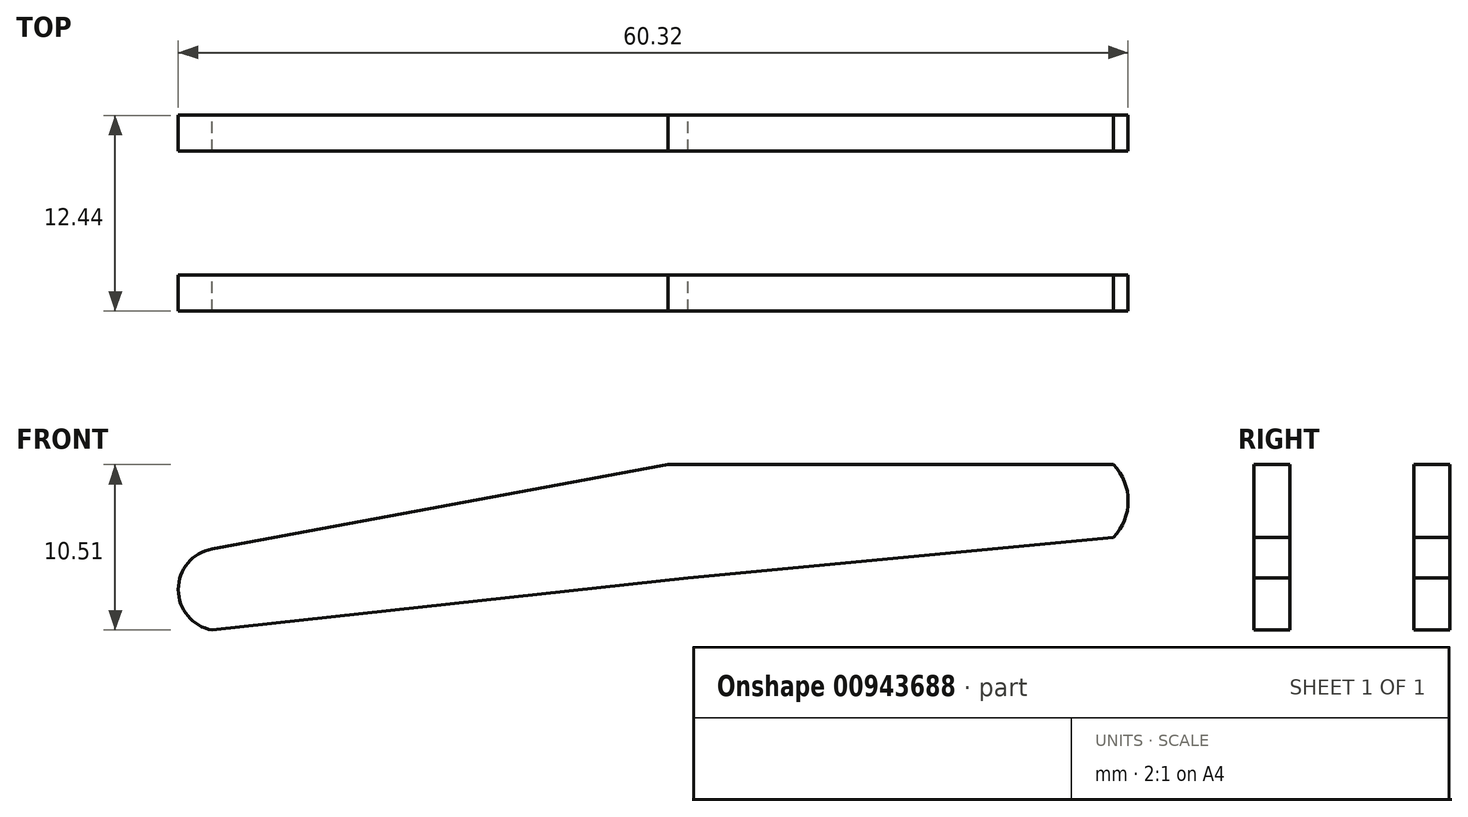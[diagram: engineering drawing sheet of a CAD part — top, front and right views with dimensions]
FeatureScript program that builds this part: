
annotation { "Feature Type Name" : "Feature", "Feature Type Description" : "" }
export const myFeature = defineFeature(function(context is Context, id is Id, definition is map)
    precondition{}
    {
        {
            var Q0;
            Q0=qCreatedBy(makeId("Front.planeOp"),FACE);
            var sketch = newSketch(context, id + "F0", { "sketchPlane" : qUnion([Q0])});
            skLineSegment(sketch, "E0", {"start": v(-57.24, -15.95) * mm, "end": v(-28.3, -10.6) * mm});
            skLineSegment(sketch, "E1", {"start": v(0, -10.6) * mm, "end": v(-28.3, -10.6) * mm});
            skLineSegment(sketch, "E2", {"start": v(-57.24, -21.1) * mm, "end": v(-27, -17.8) * mm});
            skLineSegment(sketch, "E3", {"start": v(-27, -17.8) * mm, "end": v(0, -15.2) * mm});
            skArc(sketch, "E4", {"start": v(-57.24, -15.95) * mm, "mid": v(-59.4, -18.53) * mm, "end": v(-57.24, -21.1) * mm});
            skArc(sketch, "E5", {"start": v(0, -15.2) * mm, "mid": v(0.93, -12.9) * mm, "end": v(0, -10.6) * mm});
            skSolve(sketch);
        }
        {
            var Q0;
            Q0=makeQuery(id+"F0.imprint","IMPRINT",FACE,{"disambiguationData":[TD([[makeQuery(id+"F0.imprint","IMPRINT",EDGE,{"derivedFrom":sQuery(id+"F0.wireOp",EDGE,"E0")}),-1.0]])]});
            extrude(context, id + "F1", {"entities" : qUnion([Q0]), "endBound" : BoundingType.SYMMETRIC, "depth" : 2.3 * mm, "offsetDistance" : 25.4 * mm});
        }
        {
            var Q0;
            Q0=makeQuery(id+"F1.opExtrude","SWEPT_BODY",BODY,{"disambiguationData":[OSD([sQuery(id+"F0.wireOp",EDGE,"E0"),sQuery(id+"F0.wireOp",EDGE,"E1"),sQuery(id+"F0.wireOp",EDGE,"E2"),sQuery(id+"F0.wireOp",EDGE,"E3"),sQuery(id+"F0.wireOp",EDGE,"E4"),sQuery(id+"F0.wireOp",EDGE,"E5")])]});
            transform(context, id + "F2", {"entities" : qUnion([Q0]), "transformType" : TransformType.TRANSLATION_3D, "dx" : 0 * mm, "dy" : 10.16 * mm, "dz" : 0 * mm, "makeCopy" : true});
        }
    });
